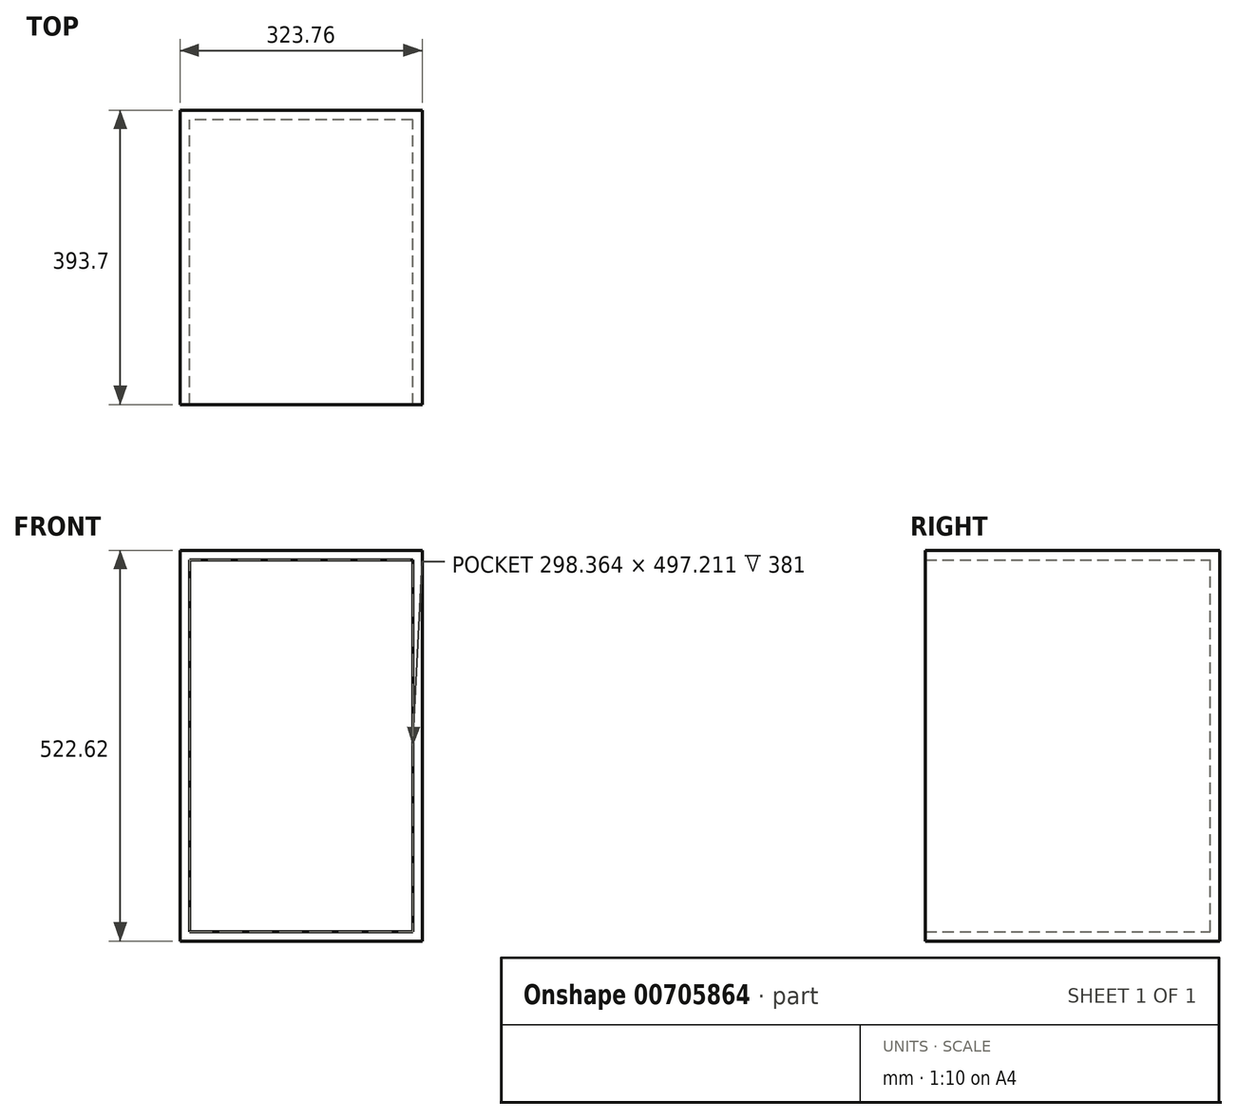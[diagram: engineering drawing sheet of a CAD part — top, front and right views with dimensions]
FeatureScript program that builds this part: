
annotation { "Feature Type Name" : "Feature", "Feature Type Description" : "" }
export const myFeature = defineFeature(function(context is Context, id is Id, definition is map)
    precondition{}
    {
        {
            var Q0;
            Q0=qCreatedBy(makeId("Front.planeOp"),FACE);
            var sketch = newSketch(context, id + "F0", { "sketchPlane" : qUnion([Q0])});
            skLineSegment(sketch, "E0.bottom", {"start": v(149.18, -248.6) * mm, "end": v(-149.18, -248.6) * mm});
            skLineSegment(sketch, "E0.top", {"start": v(149.18, 248.6) * mm, "end": v(-149.18, 248.6) * mm});
            skLineSegment(sketch, "E0.left", {"start": v(149.18, -248.6) * mm, "end": v(149.18, 248.6) * mm});
            skLineSegment(sketch, "E0.right", {"start": v(-149.18, -248.6) * mm, "end": v(-149.18, 248.6) * mm});
            skPoint(sketch, "E0.middle", {"position": v(0, 0) * mm});
            skSolve(sketch);
        }
        {
            var Q0;
            Q0 = qSketchRegion(id + "F0", true);
            extrude(context, id + "F1", {"entities" : qUnion([Q0]), "depth" : 381 * mm, "offsetDistance" : 25.4 * mm});
        }
        {
            var Q0;
            Q0=makeQuery(id+"F1.opExtrude","CAP_FACE",FACE,{"disambiguationData":[OSD([sQuery(id+"F0.wireOp",EDGE,"E0.bottom"),sQuery(id+"F0.wireOp",EDGE,"E0.top"),sQuery(id+"F0.wireOp",EDGE,"E0.left"),sQuery(id+"F0.wireOp",EDGE,"E0.right")])],"isStart":false});
            shell(context, id + "F2", {"entities" : qUnion([Q0]), "thickness" : 12.7 * mm, "oppositeDirection" : true});
        }
    });
